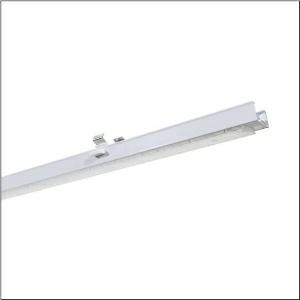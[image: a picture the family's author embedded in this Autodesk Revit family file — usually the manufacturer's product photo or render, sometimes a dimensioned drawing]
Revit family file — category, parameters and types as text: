
# Revit family: trunking_flex_31_51re12mb68b
name_source: partatom
category: Lighting Fixtures
units: mm (PartAtom-declared; Revit-internal decimal feet)

## family parameters
Cut with Voids When Loaded = No
Host = Face
Light Source = No
Part Type = Normal
Room Calculation Point = No
Round Connector Dimension = Use Diameter
Shared = No

## types (1)
- --- (1 x LED, 8000 lm, 50 W, 6500K)
    Apparent Load = 50 VA
    CIE Flux Codes = 65 91 98 99 100
    Color Rendering = 80
    Color Temperature = 6500K
    Default Elevation = 1800 mm
    Description = Trunking Flex 31, luminaire insert, of extruded aluminium section, coated, traffic white (RAL 9016), length: 1.472mm, width: 91mm, height: 53mm, LED rated luminous flux: 8.000lm, light colour: 865, control gear: ON/OFF Multilumen, with system connector: socket, mains connection: 220..240V, AC, 50/60Hz, rated input power: 50W, luminous flux adjustable on luminaire in four steps (4130/5610/6850/8000lm), connected load according to luminous flux setting (25/34/42/50W), primary light control with lens, of plastic, primary optical cover: cover, of PMMA, light emission: direct distribution, protection rating (complete): IP20, insulation class (complete): insulation class I (protective earthing), certification: CE, UKCA, impact resistance: IK02, permissible ambient temperature for indoor applications: -20..+40°C, packaging unit: 1 piece
    Height = 58 mm
    Lamp = 1 x LED
    Lamp Light Flux = 8000 lm
    Lamp Power = 50 W
    Lamp count = 1
    Length = 1472 mm
    Luminous efficacy = 160 lm/W
    Manufacturer = Siteco
    ModVariant = No
    Model = 51RE12MB68B
    Mounting Place = Ceiling
    Mounting Type = Pendant
    Number of Poles = 1
    OnlyDefault = Yes
    Power Factor = 1
    Product Name = Trunking Flex 31
    Product group = luminaire insert | ceiling pendant
    ProductGroupID = 902
    Protection Class = Protection class I
    Protection Degree = IP 20
    RLX_Detail_Level = 1
    RLX_Emergency_Light_Flux = 0 lm
    RLX_Emergency_Type = 0
    RLX_Emergency_Type_DB = No
    RlxData = <blob elided: 20313 chars, md5=bebda9b1>
    Socket = socket
    Standby Power = 0 W
    System Light Flux = 8000 lm
    System Power = 50 W
    Type Comments = factory setting: luminous flux: 100 % | (ON | ON) | 300 mA
    Type Image = l_1266702.jpg
    URL = http://relux.com
    VarID = @adj_079203
    Voltage = 0 V
    Weight = 0.00 kg
    Width = 65 mm

## geometry (parser evidence)
native form markers: Blend x4, Sweep x9
no freeform markers — native parametric forms only
